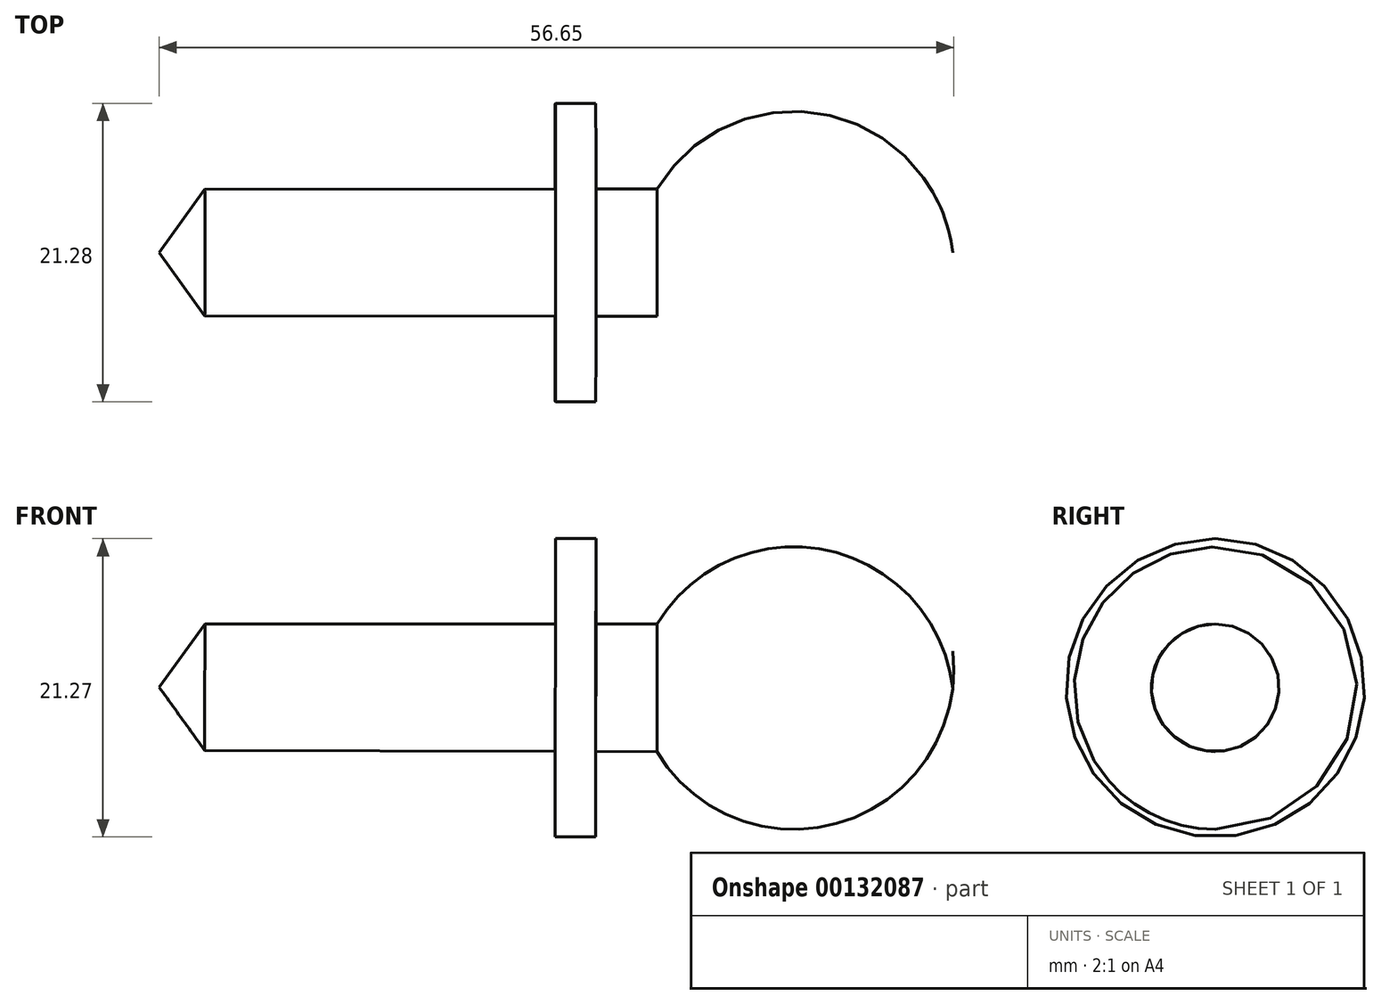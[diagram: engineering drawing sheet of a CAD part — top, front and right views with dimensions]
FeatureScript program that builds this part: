
annotation { "Feature Type Name" : "Feature", "Feature Type Description" : "" }
export const myFeature = defineFeature(function(context is Context, id is Id, definition is map)
    precondition{}
    {
        {
            var Q0;
            Q0=qCreatedBy(makeId("Front.planeOp"),FACE);
            var sketch = newSketch(context, id + "F0", { "sketchPlane" : qUnion([Q0])});
            skLineSegment(sketch, "E0", {"start": v(-65.72, 0) * mm, "end": v(-62.46, 4.5) * mm});
            skLineSegment(sketch, "E1", {"start": v(-62.46, 4.5) * mm, "end": v(-37.46, 4.5) * mm});
            skLineSegment(sketch, "E2", {"start": v(-37.46, 4.5) * mm, "end": v(-37.46, 10.6) * mm});
            skLineSegment(sketch, "E3", {"start": v(-37.46, 10.6) * mm, "end": v(-34.58, 10.6) * mm});
            skLineSegment(sketch, "E4", {"start": v(-34.58, 10.6) * mm, "end": v(-34.58, 4.5) * mm});
            skLineSegment(sketch, "E5", {"start": v(-34.58, 4.5) * mm, "end": v(-30.23, 4.5) * mm});
            skLineSegment(sketch, "E6", {"start": v(-30.23, 4.5) * mm, "end": v(-30.23, 0) * mm});
            skArc(sketch, "E7", {"start": v(-9.15, -0.08) * mm, "mid": v(-18.05, 9.75) * mm, "end": v(-30.23, 4.5) * mm});
            skPoint(sketch, "E8.center.orphan", {"position": v(-20.54, 0) * mm});
            skPoint(sketch, "E9.orphan", {"position": v(-34.58, 0) * mm});
            skLineSegment(sketch, "E10", {"start": v(-65.72, 0) * mm, "end": v(-9.15, -0.08) * mm});
            skSolve(sketch);
        }
        {
            var Q0;
            Q0=makeQuery(id+"F0.imprint","IMPRINT",FACE,{"disambiguationData":[TD([[makeQuery(id+"F0.imprint","IMPRINT",EDGE,{"derivedFrom":sQuery(id+"F0.wireOp",EDGE,"E0")}),-1.0]])]});
            var Q1;
            Q1=sQuery(id+"F0.wireOp",EDGE,"E10");
            revolve(context, id + "F1", {"entities" : qUnion([Q0]), "axis" : qUnion([Q1]), "revolveType" : RevolveType.FULL});
        }
    });
